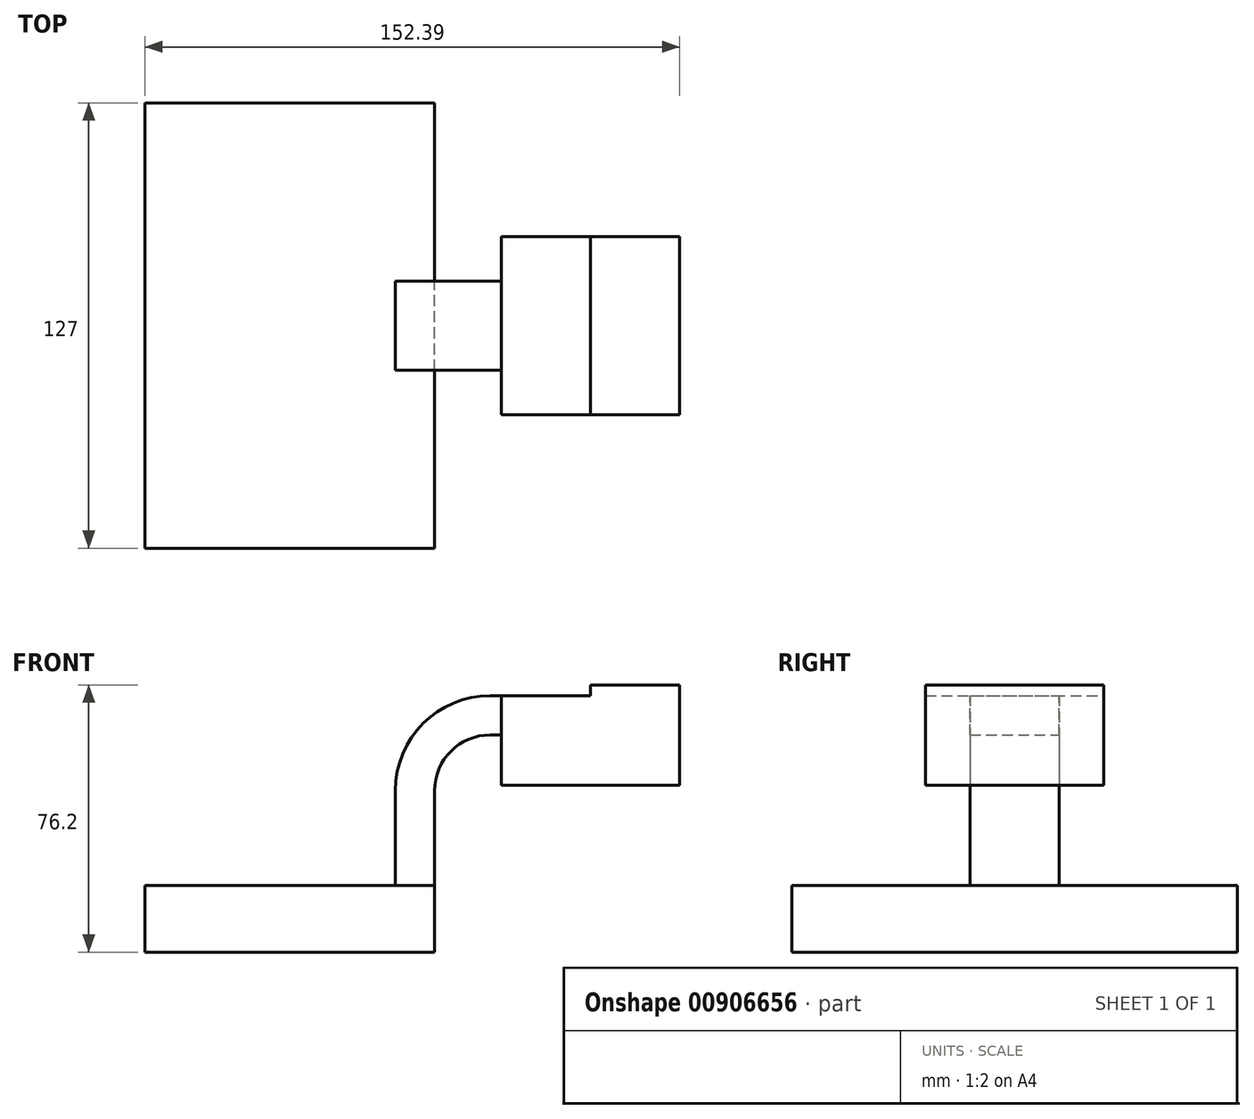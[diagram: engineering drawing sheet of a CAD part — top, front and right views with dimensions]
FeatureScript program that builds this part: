
annotation { "Feature Type Name" : "Feature", "Feature Type Description" : "" }
export const myFeature = defineFeature(function(context is Context, id is Id, definition is map)
    precondition{}
    {
        {
            var Q0;
            Q0=qCreatedBy(makeId("Front.planeOp"),FACE);
            var sketch = newSketch(context, id + "F0", { "sketchPlane" : qUnion([Q0])});
            skLineSegment(sketch, "E0.bottom", {"start": v(-41.28, 9.52) * mm, "end": v(41.28, 9.53) * mm});
            skLineSegment(sketch, "E0.top", {"start": v(-41.28, -9.53) * mm, "end": v(41.28, -9.53) * mm});
            skLineSegment(sketch, "E0.left", {"start": v(-41.28, 9.52) * mm, "end": v(-41.28, -9.53) * mm});
            skLineSegment(sketch, "E0.right", {"start": v(41.28, 9.53) * mm, "end": v(41.28, -9.52) * mm});
            skPoint(sketch, "E0.middle", {"position": v(0, 0) * mm});
            skLineSegment(sketch, "E1.bottom", {"start": v(60.32, 38.1) * mm, "end": v(111.12, 38.1) * mm});
            skLineSegment(sketch, "E1.top", {"start": v(60.32, 66.68) * mm, "end": v(111.12, 66.68) * mm});
            skLineSegment(sketch, "E1.left", {"start": v(60.32, 38.1) * mm, "end": v(60.32, 66.68) * mm});
            skLineSegment(sketch, "E1.right", {"start": v(111.12, 38.1) * mm, "end": v(111.12, 66.68) * mm});
            skPoint(sketch, "E1.middle", {"position": v(85.72, 52.39) * mm});
            skLineSegment(sketch, "E2", {"start": v(41.27, 9.53) * mm, "end": v(41.27, 36.53) * mm});
            skArc(sketch, "E3", {"start": v(41.27, 36.53) * mm, "mid": v(45.92, 47.75) * mm, "end": v(57.15, 52.4) * mm});
            skLineSegment(sketch, "E4", {"start": v(85.72, 38.1) * mm, "end": v(85.72, 66.68) * mm});
            skLineSegment(sketch, "E5", {"start": v(57.15, 52.4) * mm, "end": v(85.72, 52.4) * mm});
            skLineSegment(sketch, "E6.0", {"start": v(57.15, 63.59) * mm, "end": v(85.72, 63.59) * mm});
            skArc(sketch, "E6.1", {"start": v(30.09, 36.53) * mm, "mid": v(38.01, 55.66) * mm, "end": v(57.15, 63.59) * mm});
            skLineSegment(sketch, "E6.2", {"start": v(30.09, 9.53) * mm, "end": v(30.09, 36.53) * mm});
            skSolve(sketch);
        }
        {
            var Q0;
            Q0=makeQuery(id+"F0.imprint","IMPRINT",FACE,{"disambiguationData":[TD([[makeQuery(id+"F0.imprint","IMPRINT",EDGE,{"derivedFrom":sQuery(id+"F0.wireOp",EDGE,"E0.top")}),1.0]])]});
            extrude(context, id + "F1", {"entities" : qUnion([Q0]), "endBound" : BoundingType.SYMMETRIC, "depth" : 127 * mm, "offsetDistance" : 25.4 * mm});
        }
        {
            var Q0;
            {var subQ4=sQuery(id+"F0.wireOp",EDGE,"E1.right");Q0=makeQuery(id+"F0.imprint","IMPRINT",FACE,{"disambiguationData":[TD([[makeQuery(id+"F0.imprint","IMPRINT",EDGE,{"derivedFrom":subQ4}),1.0]])]});}
            var Q1;
            {var subQ0=sQuery(id+"F0.wireOp",EDGE,"E1.left");var subQ1=sQuery(id+"F0.wireOp",EDGE,"E1.bottom");var subQ2=makeQuery(id+"F0.imprint","INTERSECT",VERTEX,{"derivedFrom":[subQ1,subQ0]});Q1=makeQuery(id+"F0.imprint","IMPRINT",FACE,{"disambiguationData":[TD([[makeQuery(id+"F0.imprint","IMPRINT",EDGE,{"disambiguationData":[TD([[subQ2,-1.0]])],"derivedFrom":subQ1}),1.0]])]});}
            var Q2;
            {var subQ0=sQuery(id+"F0.wireOp",EDGE,"E5");var subQ1=sQuery(id+"F0.wireOp",EDGE,"E1.left");var subQ2=makeQuery(id+"F0.imprint","INTERSECT",VERTEX,{"derivedFrom":[subQ1,subQ0]});Q2=makeQuery(id+"F0.imprint","IMPRINT",FACE,{"disambiguationData":[TD([[makeQuery(id+"F0.imprint","IMPRINT",EDGE,{"disambiguationData":[TD([[subQ2,-1.0]])],"derivedFrom":subQ1}),-1.0]])]});}
            extrude(context, id + "F2", {"entities" : qUnion([Q0, Q1, Q2]), "endBound" : BoundingType.SYMMETRIC, "depth" : 50.8 * mm, "offsetDistance" : 25.4 * mm});
        }
        {
            var Q0;
            {var subQ1=sQuery(id+"F0.wireOp",EDGE,"E2");Q0=makeQuery(id+"F0.imprint","IMPRINT",FACE,{"disambiguationData":[TD([[makeQuery(id+"F0.imprint","IMPRINT",EDGE,{"derivedFrom":subQ1}),1.0]])]});}
            extrude(context, id + "F3", {"entities" : qUnion([Q0]), "endBound" : BoundingType.SYMMETRIC, "depth" : 25.4 * mm, "offsetDistance" : 25.4 * mm});
        }
    });
